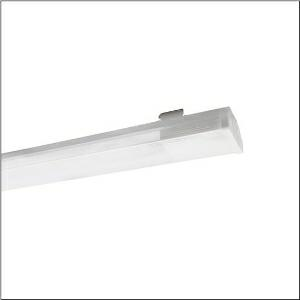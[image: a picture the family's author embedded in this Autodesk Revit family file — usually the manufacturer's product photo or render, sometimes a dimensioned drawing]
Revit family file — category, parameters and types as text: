
# Revit family: modario_r__31_gen_2_53bm8127u4l3d2_2c8d
name_source: partatom
category: Lighting Fixtures
units: mm (PartAtom-declared; Revit-internal decimal feet)

## family parameters
Cut with Voids When Loaded = No
Host = Face
Light Source = No
Part Type = Normal
Room Calculation Point = No
Round Connector Dimension = Use Diameter
Shared = No

## types (1)
- Modario® 31 Gen.2 (1 x LED, 23600 lm, 126 W, 4000K)
    Apparent Load = 126 VA
    CIE Flux Codes = 47 80 95 93 100
    Color Rendering = 80
    Color Temperature = 4000K
    Default Elevation = 1800 mm
    Description = Modario® 31 Gen.2, luminaire insert, of sheet steel, coil coated, white, length: 2.392mm, width: 81mm, height: 82mm, 8x system unit, system units: 299mm, LED rated luminous flux: 23.600lm, light colour: 840, control gear: ON/OFF, with plug, 3-pole, with phase selection, mains connection: 220..240V, AC, 50/60Hz, rated input power: 126W, through-wiring accessed according to module size, primary optical cover: cover, of PMMA, light emission: direct distribution, primary light characteristic: symmetric, protection rating (complete): IP20, protection rating (LED compartment): IP50, insulation class (complete): insulation class I (protective earthing), certification: CE, ENEC, VDE, UKCA, impact resistance: IK03, permissible ambient temperature for indoor applications: -40..+35°C, corresponds to IFS (International Featured Standards) requirements for safety and quality in the food industry, reducing of maximum allowable ambient temperature of 5°C with ceiling mounting, packaging unit: 1 piece
    Height = 92 mm
    Lamp = 1 x LED
    Lamp Light Flux = 23600 lm
    Lamp Power = 126 W
    Lamp count = 1
    Length = 2392 mm
    Luminous efficacy = 187 lm/W
    Manufacturer = Siteco
    ModVariant = No
    Model = 53BM8127U4L3D2
    Mounting Place = Ceiling
    Mounting Type = Pendant
    Number of Poles = 1
    OnlyDefault = Yes
    Power Factor = 1
    Product Name = Modario® 31 Gen.2
    Product group = luminaire insert | ceiling pendant
    ProductGroupID = 902
    Protection Class = Protection class I
    Protection Degree = IP 20
    RLX_Detail_Level = 1
    RLX_Emergency_Light_Flux = 0 lm
    RLX_Emergency_Type = 0
    RLX_Emergency_Type_DB = No
    RlxData = <blob elided: 34561 chars, md5=2a62180d>
    Socket = socket
    Standby Power = 0 W
    System Light Flux = 23600 lm
    System Power = 126 W
    Type Comments = Product without accessories
    Type Image = l_1341883.jpg
    URL = http://relux.com
    VarID = ---
    Voltage = 0 V
    Weight = 0.00 kg
    Width = 81 mm

## geometry (parser evidence)
native form markers: Blend x4, Sweep x12
no freeform markers — native parametric forms only
